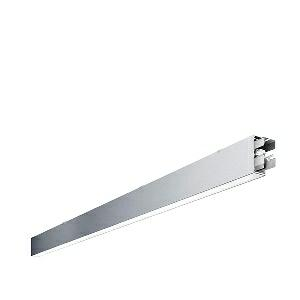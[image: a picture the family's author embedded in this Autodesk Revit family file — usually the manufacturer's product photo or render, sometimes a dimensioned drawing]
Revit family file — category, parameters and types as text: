
# Revit family: dotoo_line_-_dla_3000_840_d_sta_00807958_e062
name_source: partatom
category: Lighting Fixtures
units: mm (PartAtom-declared; Revit-internal decimal feet)

## family parameters
Cut with Voids When Loaded = No
Host = Face
Light Source = No
Part Type = Normal
Room Calculation Point = No
Round Connector Dimension = Use Diameter
Shared = No

## types (1)
- DOTOO.line - DLA 3000/840/D STA (1 x LED, 2750 lm, 4000K)
    Apparent Load = 26 VA
    Approval mark = CE
    CIE Flux Codes = 67 91 98 100 100
    Color Rendering = 80-89
    Color Temperature = 4000K
    Control Gear = Electronic ballast
    Default Elevation = 1800 mm
    Description = DLA 3000/840/D|Surface-mounted luminaire.|light source: LED|work equipment: Adjustable electronic ballast, digital DALI|connected load: 220-240 V, 50/60 Hz|Power consumption: approx. 26 W|luminous flux: 2750 lm|luminous efficacy: 105 lm/W|light distribution: Direct|colour temperature: Cold white, ca. 4000 K|class of protection: I|technology: Continuously dimmable|mains lead: Connector|glare control: Prism aperture|special features: DALI Load 1x, TouchDIM - dimming via standard switch, Through-wired, up to 18 m on one mains connection, Flicker-free, Suitable as emergency lighting, Start luminaire with mains connection, Mechanical and electrical connection of the individual modules without tools|
    Frequency = 50 Hz
    Height = 110 mm
    Lamp = 1 x LED
    Lamp Light Flux = 2750 lm
    Lamp count = 1
    Length = 2250 mm
    Luminous efficacy = 106 lm/W
    Manufacturer = Waldmann
    ModVariant = No
    Model = 00807958
    Mounting Place = Ceiling
    Mounting Type = Surface mounted
    Number of Poles = 1
    OnlyDefault = Yes
    Power Factor = 1
    Product Name = DOTOO.line - DLA 3000/840/D STA
    Product group = Ceiling mounted luminaire
    ProductGroupID = 3
    Protection Class = Protection class I
    Protection Degree = IP 40
    RLX_Detail_Level = 1
    RLX_Emergency_Light_Flux = 0 lm
    RLX_Emergency_Type = 0
    RLX_Emergency_Type_DB = No
    RlxData = <blob elided: 22717 chars, md5=62b5b5d7>
    Socket = socket
    Standby Power = 0 W
    System Light Flux = 2750 lm
    System Power = 26 W
    Type Comments = Product without accessories
    Type Image = 114381000-00807958.jpg
    URL = http://relux.com
    VarID = ---
    Voltage = 230 V
    Voltage Range = 220-240 V
    Weight = 0.00 kg
    Width = 60 mm

## geometry (parser evidence)
native form markers: Blend x4, Sweep x12
no freeform markers — native parametric forms only
